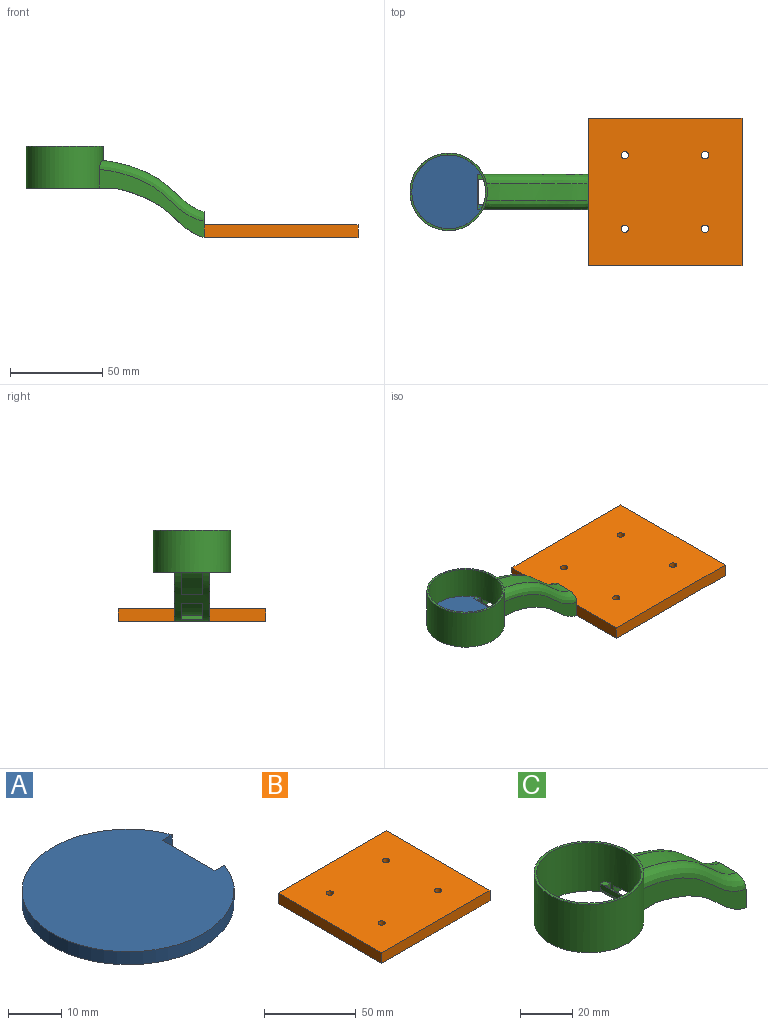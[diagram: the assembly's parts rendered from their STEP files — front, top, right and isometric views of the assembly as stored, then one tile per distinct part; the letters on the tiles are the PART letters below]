
ASSEMBLY  parts=3 mates=2
PART A: 6 faces, bbox 38.7x40x3 mm
  f0: plane 3x2.56mm, normal (0,-1,0), area 7.7mm2, adj f1,f3,f4,f5
  f1: cylinder r=20mm len=40mm, axis (0,0,-1), area 334.1mm2, adj f0,f2,f4,f5
  f2: plane 3x2.56mm, normal (0,1,0), area 7.7mm2, adj f1,f3,f4,f5
  f3: plane 14x3mm, normal (1,0,0), area 42mm2, adj f0,f2,f4,f5
  f4: plane 40x38.74mm, normal (0,0,1), area 1208.9mm2, adj f0,f1,f2,f3
  f5: plane 40x38.74mm, normal (0,0,-1), area 1208.9mm2, adj f0,f1,f2,f3
PART B: 10 faces, bbox 83.5x80x7 mm
  f0: plane 80x7mm, normal (1,0,0), area 560mm2, adj f1,f6,f8,f9
  f1: plane 83.51x7mm, normal (0,1,0), area 584.6mm2, adj f0,f2,f8,f9
  f2: plane 80x7mm, normal (-1,0,0), area 560mm2, adj f1,f6,f8,f9
  f3: cylinder r=2mm len=7mm, axis (0,0,-1), area 88mm2, adj f8,f9
  f4: cylinder r=2mm len=7mm, axis (0,0,-1), area 88mm2, adj f8,f9
  f5: cylinder r=2mm len=7mm, axis (0,0,-1), area 88mm2, adj f8,f9
  f6: plane 83.51x7mm, normal (0,-1,0), area 584.6mm2, adj f0,f2,f8,f9
  f7: cylinder r=2mm len=7mm, axis (0,0,-1), area 88mm2, adj f8,f9
  f8: plane 83.51x80mm, normal (0,0,1), area 6630.5mm2, adj f0,f1,f2,f3,f4,f5,f6,f7
  f9: plane 83.51x80mm, normal (0,0,-1), area 6630.5mm2, adj f0,f1,f2,f3,f4,f5,f6,f7
PART C: 36 faces, bbox 98.7x42.7x50.2 mm
  f0: plane 8.39x3.64mm, normal (0,0,-1), area 27.3mm2, adj f14,f15,f22,f25
  f1: cylinder r=20mm len=40mm, axis (0,0,-1), area 2765.1mm2, adj f3,f4,f6,f8,f13,f14,f24,f25
  f2: plane 8.39x3.64mm, normal (0,0,-1), area 27.3mm2, adj f14,f16,f22,f27
  f3: plane 5.01x2.02mm, normal (0,-1,0), area 8.2mm2, adj f1,f5,f9,f10,f11,f23,f24
  f4: plane 5.01x2.02mm, normal (0,1,0), area 8.2mm2, adj f1,f5,f17,f18,f19,f23,f24
  f5: plane 19x2.63mm, normal (-1,0,0), area 50mm2, adj f3,f4,f23,f24
  f6: plane 5.01x2.56mm, normal (0,-1,0), area 11.8mm2, adj f1,f7,f17,f18,f19,f23,f24
  f7: plane 14x3.75mm, normal (1,0,0), area 52.5mm2, adj f6,f8,f23,f24
  f8: plane 5.01x2.56mm, normal (0,1,0), area 11.8mm2, adj f1,f7,f9,f10,f11,f23,f24
  f9: plane 2.53x1.67mm, normal (0,0,-1), area 2.8mm2, adj f3,f8,f10,f14
  f10: plane 2.5x1.02mm, normal (-1,0,0), area 2.6mm2, adj f3,f8,f9,f11
  f11: bspline ~19x6mm, area 0.2mm2, adj f3,f8,f10,f23
  f12: cylinder r=21mm len=42mm, axis (0,0,-1), area 2714.2mm2, adj f13,f14,f15,f16,f20,f34,f35
  f13: plane 42x42mm, normal (0,0,1), area 128.8mm2, adj f1,f12
  f14: plane 42.01x41.18mm, normal (0,0,-1), area 116.9mm2, adj f0,f1,f2,f9,f12,f17,f25,f27
  f15: plane 56.88x36.9mm, normal (0,1,0), area 477.4mm2, adj f0,f12,f21,f22,f35
  f16: plane 56.88x36.9mm, normal (0,-1,0), area 477.4mm2, adj f2,f12,f21,f22,f34
  f17: plane 2.53x1.67mm, normal (0,0,-1), area 2.8mm2, adj f4,f6,f14,f18
  f18: plane 2.5x1.02mm, normal (-1,0,0), area 2.6mm2, adj f4,f6,f17,f19
  f19: bspline ~19x6mm, area 0.2mm2, adj f4,f6,f18,f23
  f20: bspline ~60x27.95mm, area 566.8mm2, adj f12,f21,f34,f35
  f21: plane 19.48x14.48mm, normal (1,0,0), area 255mm2, adj f15,f16,f20,f22,f34,f35
  f22: bspline ~49.07x26.98mm, area 529.9mm2, adj f0,f2,f15,f16,f21,f25,f27,f29
  f23: cylinder r=1.36mm len=19mm, axis (0,1,0), area 29.4mm2, adj f3,f4,f5,f6,f7,f8,f11,f19
  f24: plane 19x3.15mm, normal (0,0,1), area 21.3mm2, adj f1,f3,f4,f5,f6,f7,f8
  f25: plane 36.34x16.73mm, normal (0,-1,0), area 80mm2, adj f0,f1,f14,f22,f26,f28,f29
  f26: plane 11.8x3.59mm, normal (0,0,-1), area 35.3mm2, adj f1,f25,f27,f28
  f27: plane 36.32x16.71mm, normal (0,1,0), area 81mm2, adj f1,f2,f14,f22,f26,f28,f29
  f28: plane 11.8x0.38mm, normal (-1,0,0), area 4.5mm2, adj f25,f26,f27,f29
  f29: bspline ~37.54x19.62mm, area 427.8mm2, adj f22,f25,f27,f28
  f30: bspline ~18.51x11.8mm, area 173.7mm2, adj f22,f31,f32,f33
  f31: plane 11.8x2.38mm, normal (-0.97,0,0.26), area 29mm2, adj f22,f30,f32,f33
  f32: plane 13.58x9.64mm, normal (0,-1,0), area 16.6mm2, adj f22,f30,f31
  f33: plane 13.75x9.8mm, normal (0,1,0), area 16.9mm2, adj f22,f30,f31
  f34: bspline ~58.56x33.09mm, area 502.8mm2, adj f12,f16,f20,f21
  f35: bspline ~58.56x33.09mm, area 502.8mm2, adj f12,f15,f20,f21
PLACE A t=(100.01,121.76,99.53)mm
PLACE B t=(217.35,121.76,69.66)mm
PLACE C t=(100.01,121.76,99.53)mm
MATE fastened C.f21 <-> B.f2  axis (1,0,0) through (175.6,121.76,69.66)mm
MATE fastened A.f4 <-> C.f24  axis (0,0,1) through (116.19,121.76,101.53)mm
